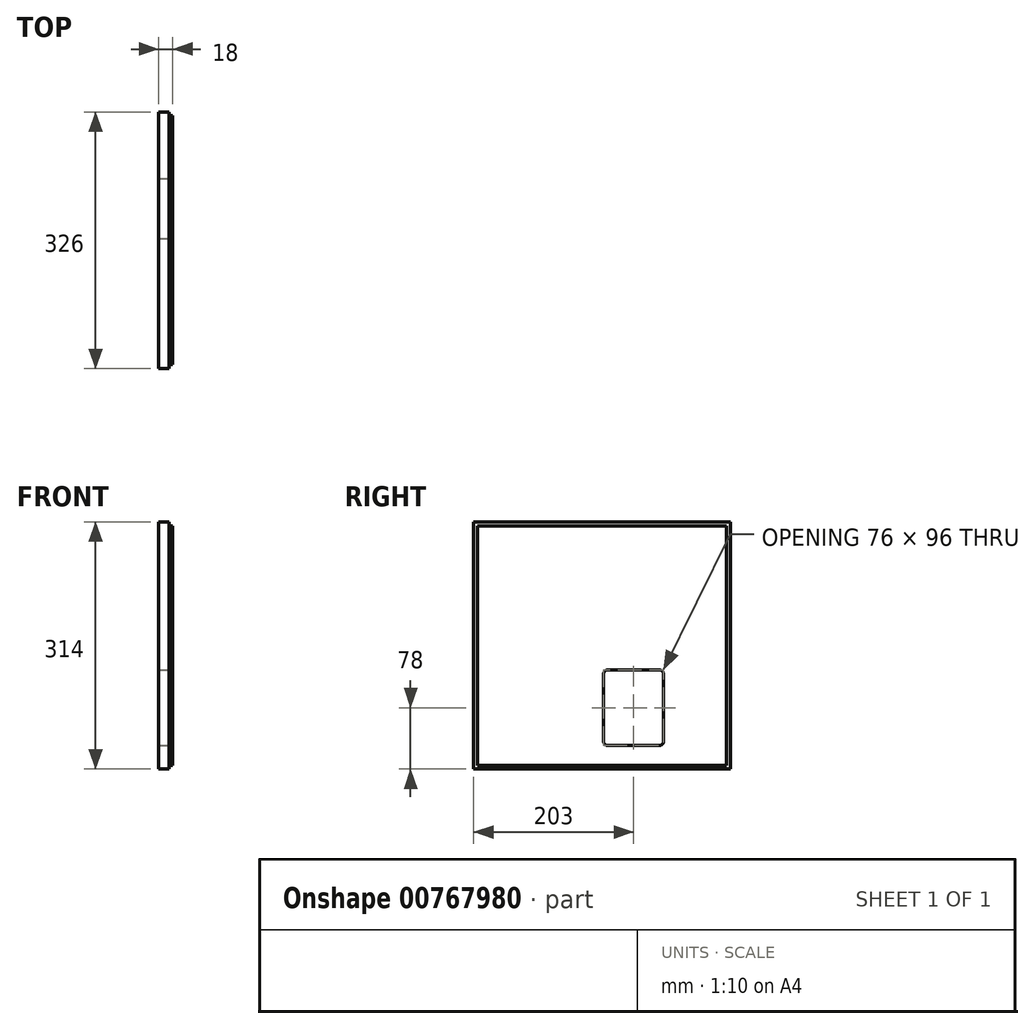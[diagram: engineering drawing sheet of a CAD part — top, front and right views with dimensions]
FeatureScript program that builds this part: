
annotation { "Feature Type Name" : "Feature", "Feature Type Description" : "" }
export const myFeature = defineFeature(function(context is Context, id is Id, definition is map)
    precondition{}
    {
        {
            var Q0;
            Q0=qCreatedBy(makeId("Right.planeOp"),FACE);
            var sketch = newSketch(context, id + "F0", { "sketchPlane" : qUnion([Q0])});
            skLineSegment(sketch, "E0.bottom", {"start": v(-163, 157) * mm, "end": v(163, 157) * mm});
            skLineSegment(sketch, "E0.top", {"start": v(-163, -157) * mm, "end": v(163, -157) * mm});
            skLineSegment(sketch, "E0.left", {"start": v(-163, 157) * mm, "end": v(-163, -157) * mm});
            skLineSegment(sketch, "E0.right", {"start": v(163, 157) * mm, "end": v(163, -157) * mm});
            skPoint(sketch, "E0.middle", {"position": v(0, 0) * mm});
            skLineSegment(sketch, "E1.bottom", {"start": v(7, -31) * mm, "end": v(73, -31) * mm});
            skLineSegment(sketch, "E1.top", {"start": v(7, -127) * mm, "end": v(73, -127) * mm});
            skLineSegment(sketch, "E1.left", {"start": v(2, -36) * mm, "end": v(2, -122) * mm});
            skLineSegment(sketch, "E1.right", {"start": v(78, -36) * mm, "end": v(78, -122) * mm});
            skPoint(sketch, "E2.visualSharp", {"position": v(2, -31) * mm});
            skArc(sketch, "E2.filletArc", {"start": v(7, -31) * mm, "mid": v(3.46, -32.46) * mm, "end": v(2, -36) * mm});
            skPoint(sketch, "E3.visualSharp", {"position": v(78, -31) * mm});
            skArc(sketch, "E3.filletArc", {"start": v(78, -36) * mm, "mid": v(76.54, -32.46) * mm, "end": v(73, -31) * mm});
            skPoint(sketch, "E4.visualSharp", {"position": v(78, -127) * mm});
            skArc(sketch, "E4.filletArc", {"start": v(73, -127) * mm, "mid": v(76.54, -125.54) * mm, "end": v(78, -122) * mm});
            skPoint(sketch, "E5.visualSharp", {"position": v(2, -127) * mm});
            skArc(sketch, "E5.filletArc", {"start": v(2, -122) * mm, "mid": v(3.46, -125.54) * mm, "end": v(7, -127) * mm});
            skSolve(sketch);
        }
        {
            var Q0;
            Q0 = qSketchRegion(id + "F0", true);
            extrude(context, id + "F1", {"entities" : qUnion([Q0]), "oppositeDirection" : true, "depth" : 18 * mm, "offsetDistance" : 25 * mm});
        }
        {
            var Q0;
            Q0=makeQuery(id+"F1.opExtrude","CAP_FACE",FACE,{"disambiguationData":[OSD([sQuery(id+"F0.wireOp",EDGE,"E0.bottom"),sQuery(id+"F0.wireOp",EDGE,"E0.top"),sQuery(id+"F0.wireOp",EDGE,"E0.left"),sQuery(id+"F0.wireOp",EDGE,"E0.right")])],"isStart":true});
            var sketch = newSketch(context, id + "F2", { "sketchPlane" : qUnion([Q0])});
            skLineSegment(sketch, "E6.bottom", {"start": v(-163, 157) * mm, "end": v(163, 157) * mm});
            skLineSegment(sketch, "E6.top", {"start": v(-163, -157) * mm, "end": v(163, -157) * mm});
            skLineSegment(sketch, "E6.left", {"start": v(-163, 157) * mm, "end": v(-163, -157) * mm});
            skLineSegment(sketch, "E6.right", {"start": v(163, 157) * mm, "end": v(163, -157) * mm});
            skLineSegment(sketch, "E7.bottom", {"start": v(-158, 152) * mm, "end": v(158, 152) * mm});
            skLineSegment(sketch, "E7.top", {"start": v(-158, -152) * mm, "end": v(158, -152) * mm});
            skLineSegment(sketch, "E7.left", {"start": v(-158, 152) * mm, "end": v(-158, -152) * mm});
            skLineSegment(sketch, "E7.right", {"start": v(158, 152) * mm, "end": v(158, -152) * mm});
            skSolve(sketch);
        }
        {
            var Q0;
            Q0 = qSketchRegion(id + "F2", true);
            extrude(context, id + "F3", {"entities" : qUnion([Q0]), "operationType" : NewBodyOperationType.REMOVE, "oppositeDirection" : true, "depth" : 5 * mm, "offsetDistance" : 25 * mm});
        }
    });
